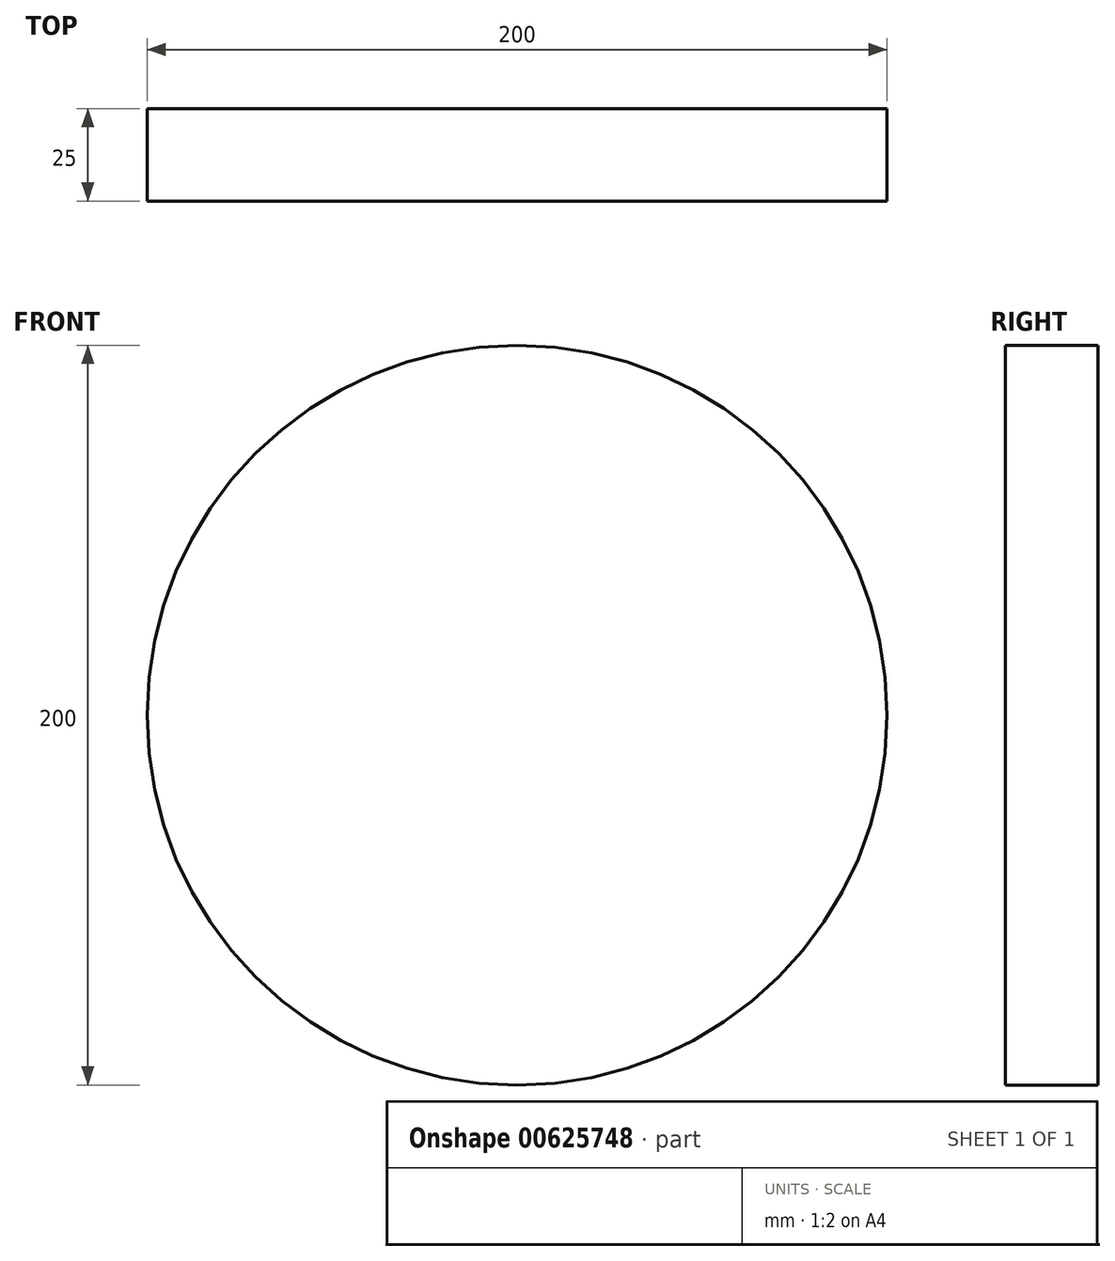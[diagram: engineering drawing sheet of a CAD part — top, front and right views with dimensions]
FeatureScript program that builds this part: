
annotation { "Feature Type Name" : "Feature", "Feature Type Description" : "" }
export const myFeature = defineFeature(function(context is Context, id is Id, definition is map)
    precondition{}
    {
        {
            var Q0;
            Q0=qCreatedBy(makeId("Front.planeOp"),FACE);
            var sketch = newSketch(context, id + "F0", { "sketchPlane" : qUnion([Q0])});
            skCircle(sketch, "E0", {"center": v(0, 0) * mm, "radius": 100 * mm});
            skSolve(sketch);
        }
        {
            var Q0;
            Q0=makeQuery(id+"F0.imprint","IMPRINT",FACE,{"disambiguationData":[TD([[makeQuery(id+"F0.imprint","IMPRINT",EDGE,{"derivedFrom":sQuery(id+"F0.wireOp",EDGE,"E0")}),1.0]])]});
            extrude(context, id + "F1", {"entities" : qUnion([Q0]), "depth" : 25 * mm, "offsetDistance" : 25 * mm});
        }
    });
